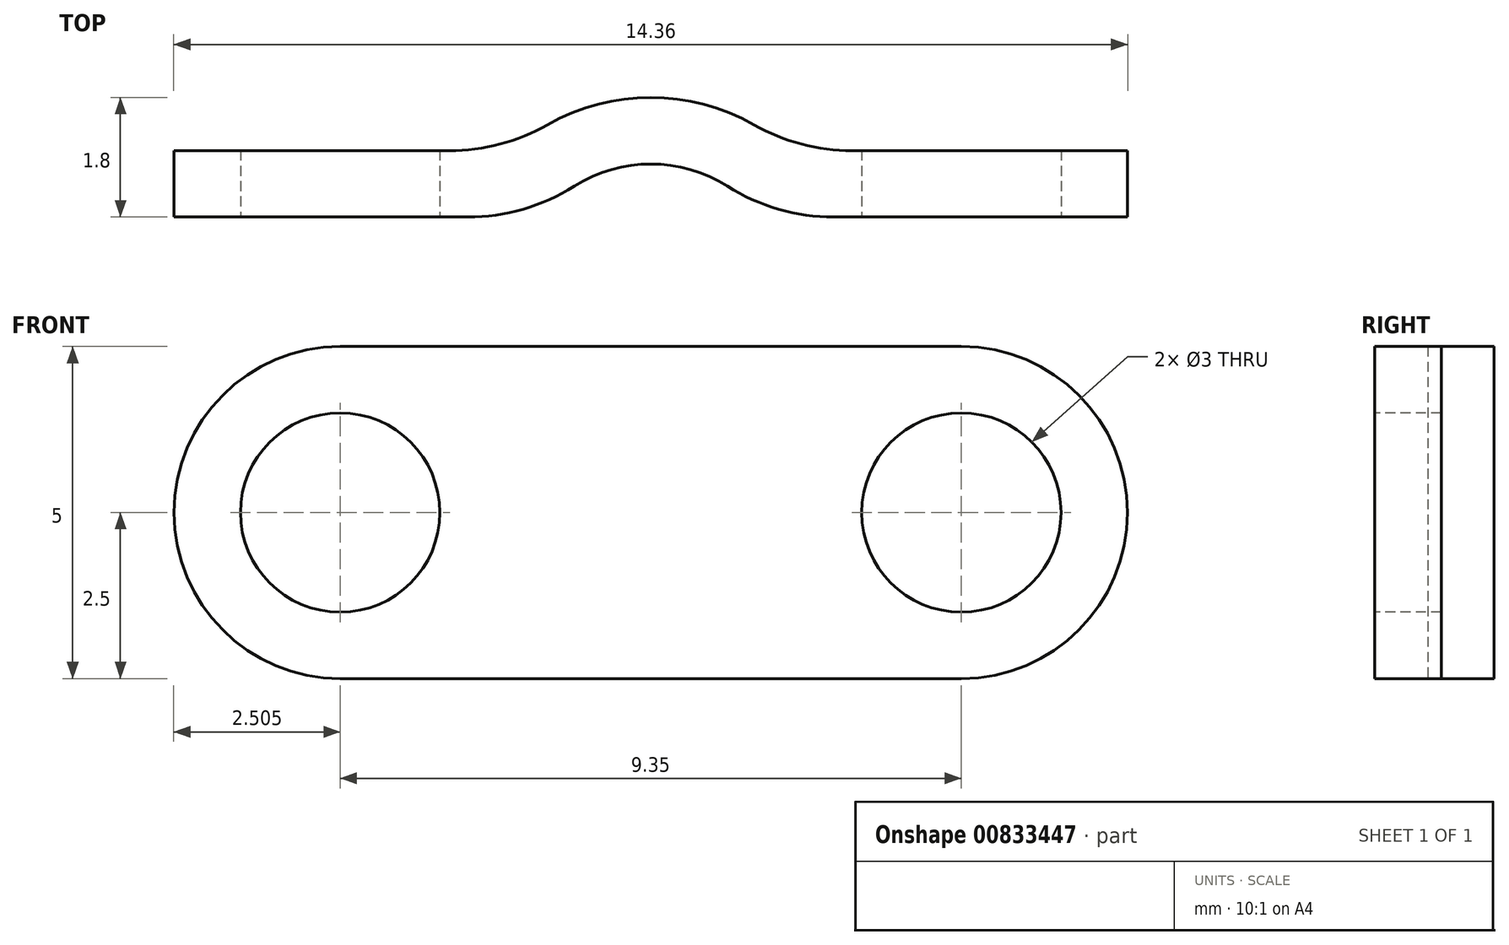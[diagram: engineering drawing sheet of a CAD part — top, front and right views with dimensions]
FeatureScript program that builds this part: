
annotation { "Feature Type Name" : "Feature", "Feature Type Description" : "" }
export const myFeature = defineFeature(function(context is Context, id is Id, definition is map)
    precondition{}
    {
        {
            var Q0;
            Q0=qCreatedBy(makeId("Top.planeOp"),FACE);
            var sketch = newSketch(context, id + "F0", { "sketchPlane" : qUnion([Q0])});
            skLineSegment(sketch, "E0", {"start": v(-4.67, 0) * mm, "end": v(4.67, 0) * mm});
            skLineSegment(sketch, "E1", {"start": v(-4.67, 0) * mm, "end": v(-6.18, 0) * mm});
            skLineSegment(sketch, "E2", {"start": v(-6.18, 0) * mm, "end": v(-7.17, 0) * mm});
            skLineSegment(sketch, "E3", {"start": v(-4.67, 0) * mm, "end": v(-3.18, 0) * mm});
            skLineSegment(sketch, "E4", {"start": v(0, 0) * mm, "end": v(0, 1.1) * mm});
            skLineSegment(sketch, "E5.MirrorCS", {"start": v(4.67, 0) * mm, "end": v(6.18, 0) * mm});
            skLineSegment(sketch, "E6.MirrorCS", {"start": v(4.67, 0) * mm, "end": v(3.18, 0) * mm});
            skLineSegment(sketch, "E7.MirrorCS", {"start": v(6.18, 0) * mm, "end": v(7.17, 0) * mm});
            skLineSegment(sketch, "E8", {"start": v(-3.18, 0) * mm, "end": v(-1.68, 0) * mm});
            skLineSegment(sketch, "E9", {"start": v(3.18, 0) * mm, "end": v(1.68, 0) * mm});
            skArc(sketch, "E10", {"start": v(1.68, 0) * mm, "mid": v(0, 0.8) * mm, "end": v(-1.68, 0) * mm});
            skLineSegment(sketch, "E11", {"start": v(-7.18, 0) * mm, "end": v(-7.18, 1) * mm});
            skLineSegment(sketch, "E12", {"start": v(-7.18, 1) * mm, "end": v(7.18, 1) * mm});
            skLineSegment(sketch, "E13", {"start": v(7.18, 1) * mm, "end": v(7.18, 0) * mm});
            skArc(sketch, "E14.0", {"start": v(2.45, 0.63) * mm, "mid": v(0, 1.8) * mm, "end": v(-2.45, 0.63) * mm});
            skSolve(sketch);
        }
        {
            var Q0;
            Q0=makeQuery(id+"F0.imprint","IMPRINT",FACE,{"disambiguationData":[TD([[makeQuery(id+"F0.imprint","IMPRINT",EDGE,{"derivedFrom":sQuery(id+"F0.wireOp",EDGE,"E1")}),-1.0]])]});
            var Q1;
            {var subQ0=sQuery(id+"F0.wireOp",EDGE,"E14.0");var subQ1=sQuery(id+"F0.wireOp",EDGE,"E12");var subQ2=makeQuery(id+"F0.imprint","INTERSECT",VERTEX,{"disambiguationData":[OD(0.0)],"derivedFrom":[subQ1,subQ0]});Q1=makeQuery(id+"F0.imprint","IMPRINT",FACE,{"disambiguationData":[TD([[makeQuery(id+"F0.imprint","IMPRINT",EDGE,{"disambiguationData":[TD([[subQ2,-1.0]])],"derivedFrom":subQ1}),1.0]])]});}
            var Q2;
            Q2=makeQuery(id+"F0.imprint","IMPRINT",FACE,{"disambiguationData":[TD([[makeQuery(id+"F0.imprint","IMPRINT",EDGE,{"derivedFrom":sQuery(id+"F0.wireOp",EDGE,"E5.MirrorCS")}),1.0]])]});
            extrude(context, id + "F1", {"entities" : qUnion([Q0, Q1, Q2]), "depth" : 2.5 * mm, "offsetDistance" : 25 * mm, "hasSecondDirection" : true, "secondDirectionOppositeDirection" : true, "secondDirectionDepth" : 2.5 * mm});
        }
        {
            var Q0;
            Q0=makeQuery(id+"F1.opExtrude","CAP_EDGE",EDGE,{"disambiguationData":[OSD([sQuery(id+"F0.wireOp",EDGE,"E13")])],"isStart":false});
            var Q1;
            Q1=makeQuery(id+"F1.opExtrude","CAP_EDGE",EDGE,{"disambiguationData":[OSD([sQuery(id+"F0.wireOp",EDGE,"E13")])],"isStart":true});
            var Q2;
            Q2=makeQuery(id+"F1.opExtrude","CAP_EDGE",EDGE,{"disambiguationData":[OSD([sQuery(id+"F0.wireOp",EDGE,"E11")])],"isStart":false});
            var Q3;
            Q3=makeQuery(id+"F1.opExtrude","CAP_EDGE",EDGE,{"disambiguationData":[OSD([sQuery(id+"F0.wireOp",EDGE,"E11")])],"isStart":true});
            fillet(context, id + "F2", {"entities" : qUnion([Q0, Q1, Q2, Q3]), "radius" : 2.5 * mm, "tangentPropagation" : true, "allowEdgeOverflow" : false});
        }
        {
            var Q0;
            Q0=makeQuery(id+"F1.opExtrude","SWEPT_FACE",FACE,{"disambiguationData":[OSD([sQuery(id+"F0.wireOp",EDGE,"E1"),sQuery(id+"F0.wireOp",EDGE,"E2"),sQuery(id+"F0.wireOp",EDGE,"E3"),sQuery(id+"F0.wireOp",EDGE,"E8")])]});
            var sketch = newSketch(context, id + "F3", { "sketchPlane" : qUnion([Q0])});
            skLineSegment(sketch, "E15", {"start": v(0, 0) * mm, "end": v(4.68, 0) * mm});
            skCircle(sketch, "E16", {"center": v(4.68, 0) * mm, "radius": 1.5 * mm});
            skLineSegment(sketch, "E17", {"start": v(0, 0) * mm, "end": v(0, 4.72) * mm});
            skCircle(sketch, "E18.MirrorC", {"center": v(-4.68, 0) * mm, "radius": 1.5 * mm});
            skSolve(sketch);
        }
        {
            var Q0;
            Q0 = qSketchRegion(id + "F3", true);
            extrude(context, id + "F4", {"entities" : qUnion([Q0]), "operationType" : NewBodyOperationType.REMOVE, "oppositeDirection" : true, "depth" : 25 * mm, "offsetDistance" : 25 * mm});
        }
        {
            var Q0;
            Q0=makeQuery(id+"F1.opExtrude","SWEPT_EDGE",EDGE,{"disambiguationData":[OSD([sQuery(id+"F0.wireOp",EDGE,"E0"),sQuery(id+"F0.wireOp",EDGE,"E9"),sQuery(id+"F0.wireOp",EDGE,"E10")])]});
            var Q1;
            Q1=makeQuery(id+"F1.opExtrude","SWEPT_EDGE",EDGE,{"disambiguationData":[OSD([sQuery(id+"F0.wireOp",EDGE,"E0"),sQuery(id+"F0.wireOp",EDGE,"E8"),sQuery(id+"F0.wireOp",EDGE,"E10")])]});
            var Q2;
            {var subQ0=sQuery(id+"F0.wireOp",EDGE,"E14.0");var subQ1=sQuery(id+"F0.wireOp",EDGE,"E12");Q2=makeQuery(id+"F1.opExtrude","SWEPT_EDGE",EDGE,{"disambiguationData":[OSD([subQ1,subQ0]),TDD([makeQuery(id+"F0.imprint","INTERSECT",VERTEX,{"disambiguationData":[OD(0.0)],"derivedFrom":[subQ1,subQ0]})])]});}
            var Q3;
            {var subQ0=sQuery(id+"F0.wireOp",EDGE,"E14.0");var subQ1=sQuery(id+"F0.wireOp",EDGE,"E12");Q3=makeQuery(id+"F1.opExtrude","SWEPT_EDGE",EDGE,{"disambiguationData":[OSD([subQ1,subQ0]),TDD([makeQuery(id+"F0.imprint","INTERSECT",VERTEX,{"disambiguationData":[OD(1.0)],"derivedFrom":[subQ1,subQ0]})])]});}
            fillet(context, id + "F5", {"entities" : qUnion([Q0, Q1, Q2, Q3]), "radius" : 3 * mm, "tangentPropagation" : true, "allowEdgeOverflow" : false});
        }
    });
